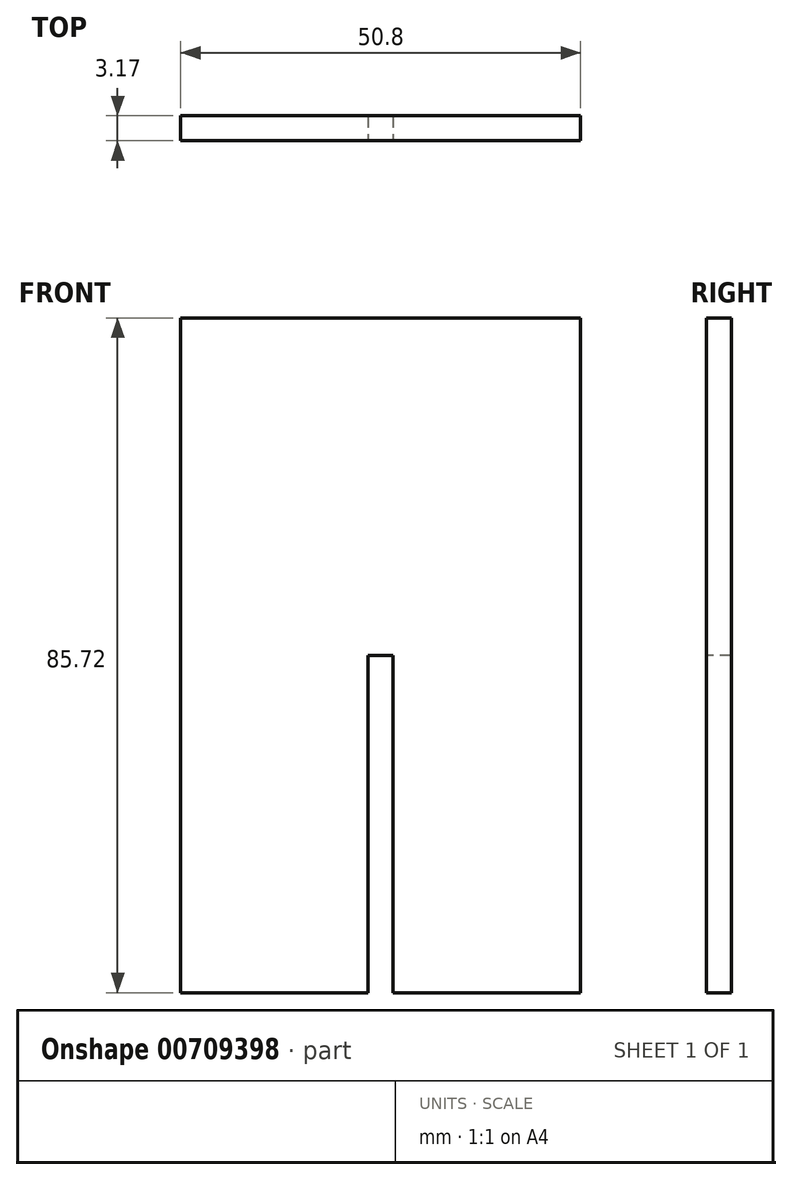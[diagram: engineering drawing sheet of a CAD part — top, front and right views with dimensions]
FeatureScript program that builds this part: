
annotation { "Feature Type Name" : "Feature", "Feature Type Description" : "" }
export const myFeature = defineFeature(function(context is Context, id is Id, definition is map)
    precondition{}
    {
        {
            var Q0;
            Q0=qCreatedBy(makeId("Front.planeOp"),FACE);
            var sketch = newSketch(context, id + "F0", { "sketchPlane" : qUnion([Q0])});
            skLineSegment(sketch, "E0.bottom", {"start": v(-25.4, 0) * mm, "end": v(25.4, 0) * mm});
            skLineSegment(sketch, "E0.top", {"start": v(-25.4, 85.72) * mm, "end": v(25.4, 85.72) * mm});
            skLineSegment(sketch, "E0.left", {"start": v(-25.4, 0) * mm, "end": v(-25.4, 85.72) * mm});
            skLineSegment(sketch, "E0.right", {"start": v(25.4, 0) * mm, "end": v(25.4, 85.72) * mm});
            skSolve(sketch);
        }
        {
            var Q0;
            Q0 = qSketchRegion(id + "F0", true);
            extrude(context, id + "F1", {"entities" : qUnion([Q0]), "depth" : 3.17 * mm, "offsetDistance" : 25.4 * mm});
        }
        {
            var Q0;
            Q0=makeQuery(id+"F1.opExtrude","CAP_FACE",FACE,{"disambiguationData":[OSD([sQuery(id+"F0.wireOp",EDGE,"E0.bottom"),sQuery(id+"F0.wireOp",EDGE,"E0.top"),sQuery(id+"F0.wireOp",EDGE,"E0.left"),sQuery(id+"F0.wireOp",EDGE,"E0.right")])],"isStart":false});
            var sketch = newSketch(context, id + "F2", { "sketchPlane" : qUnion([Q0])});
            skLineSegment(sketch, "E1.bottom", {"start": v(-1.59, 0) * mm, "end": v(1.59, 0) * mm});
            skLineSegment(sketch, "E1.top", {"start": v(-1.59, 42.86) * mm, "end": v(1.59, 42.86) * mm});
            skLineSegment(sketch, "E1.left", {"start": v(-1.59, 0) * mm, "end": v(-1.59, 42.86) * mm});
            skLineSegment(sketch, "E1.right", {"start": v(1.59, 0) * mm, "end": v(1.59, 42.86) * mm});
            skSolve(sketch);
        }
        {
            var Q0;
            Q0 = qSketchRegion(id + "F2", true);
            extrude(context, id + "F3", {"entities" : qUnion([Q0]), "operationType" : NewBodyOperationType.REMOVE, "oppositeDirection" : true, "depth" : 3.17 * mm, "offsetDistance" : 25.4 * mm});
        }
        {
            var Q0;
            Q0=makeQuery(id+"F1.opExtrude","SWEPT_BODY",BODY,{"disambiguationData":[OSD([sQuery(id+"F0.wireOp",EDGE,"E0.bottom"),sQuery(id+"F0.wireOp",EDGE,"E0.top"),sQuery(id+"F0.wireOp",EDGE,"E0.left"),sQuery(id+"F0.wireOp",EDGE,"E0.right")])]});
            transform(context, id + "F4", {"entities" : qUnion([Q0]), "transformType" : TransformType.TRANSLATION_3D, "dx" : 0 * mm, "dy" : 0 * mm, "dz" : 0 * mm, "makeCopy" : true});
        }
        {
            var Q0;
            Q0=makeQuery(id+"F4.opPattern","COPY",BODY,{"derivedFrom":makeQuery(id+"F1.opExtrude","SWEPT_BODY",BODY,{"disambiguationData":[OSD([sQuery(id+"F0.wireOp",EDGE,"E0.bottom"),sQuery(id+"F0.wireOp",EDGE,"E0.top"),sQuery(id+"F0.wireOp",EDGE,"E0.left"),sQuery(id+"F0.wireOp",EDGE,"E0.right")])]}),"instanceName":"1"});
            deleteBodies(context, id + "F5", {"entities" : qUnion([Q0])});
        }
    });
